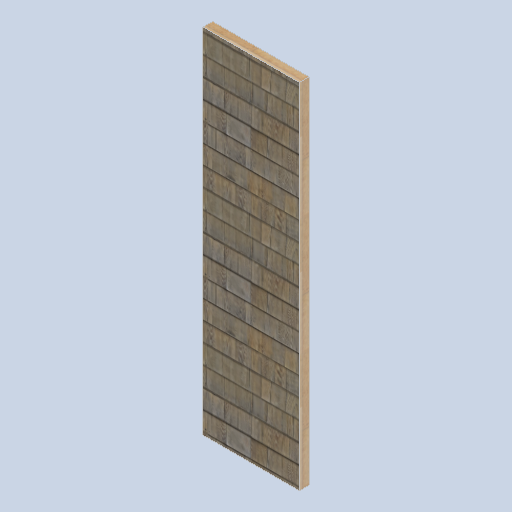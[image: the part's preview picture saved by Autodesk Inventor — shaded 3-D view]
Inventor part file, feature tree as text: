
AUTODESK INVENTOR PART (.ipt)
format: ipt  version: 2024.2 (Build 282272000, 272)  size: 365,568 bytes
history: native  units: mm
features: extrude x1, sketch x1
ambient origin geometry x8: Origin, YZ Plane, XZ Plane, XY Plane, X Axis, Y Axis, Z Axis, Center Point
bodies: Solid1 (feature_tree)
feature tree (2):
  extrude  "Extrusion1"  [1 undecoded]
  sketch  "Sketch1"  dims[d0=80.0mm d1=0.0mm]
note: 1 required parameter value undecoded (feature->parameter linkage not recoverable at this tier; creation-order binding heuristic only, values carry confidence <= 0.55)
